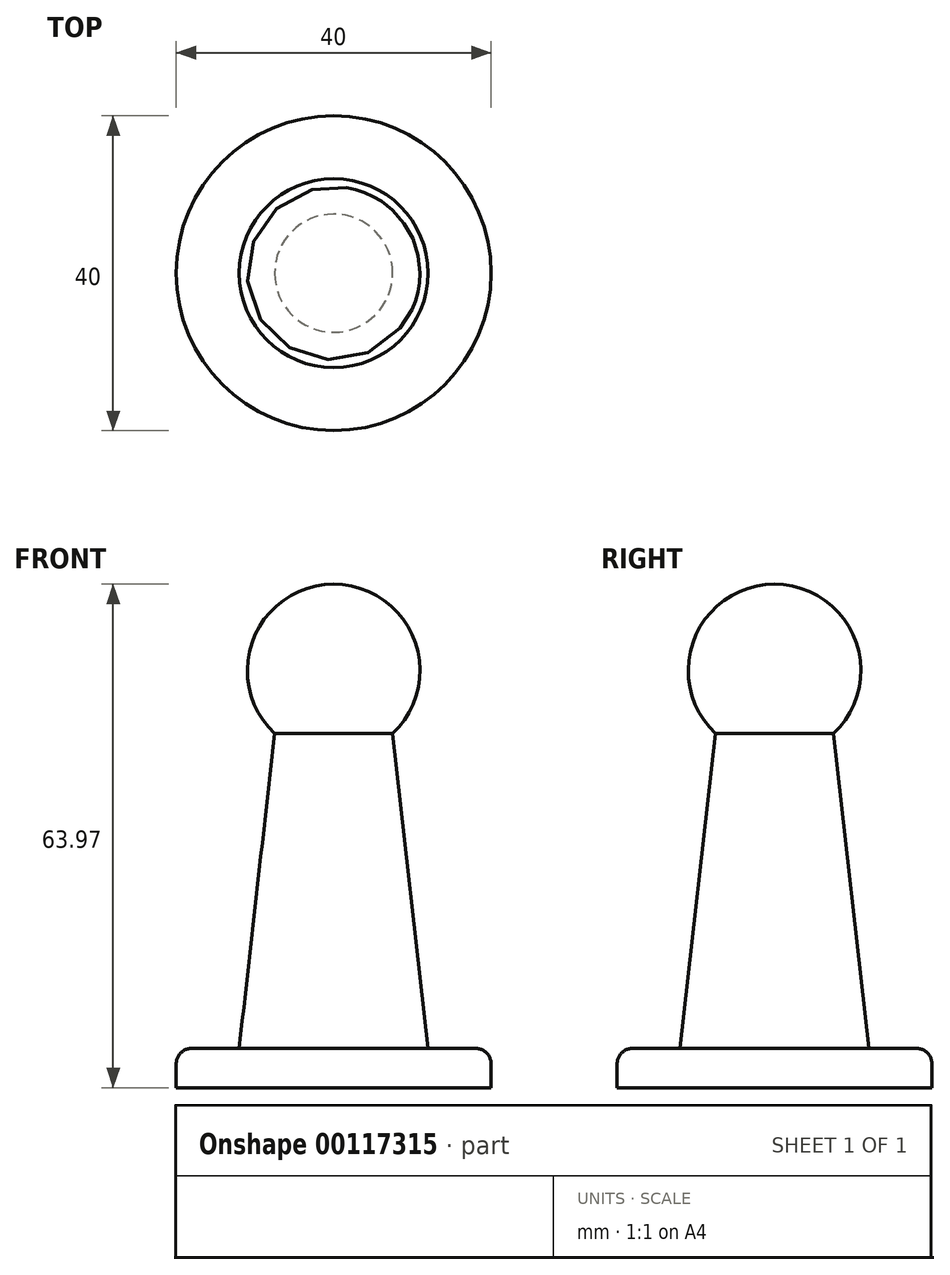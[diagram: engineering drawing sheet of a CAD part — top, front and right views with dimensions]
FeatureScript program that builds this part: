
annotation { "Feature Type Name" : "Feature", "Feature Type Description" : "" }
export const myFeature = defineFeature(function(context is Context, id is Id, definition is map)
    precondition{}
    {
        {
            var Q0;
            Q0=qCreatedBy(makeId("Front.planeOp"),FACE);
            var sketch = newSketch(context, id + "F0", { "sketchPlane" : qUnion([Q0])});
            skLineSegment(sketch, "E0.bottom", {"start": v(20, -2.5) * mm, "end": v(-20, -2.5) * mm, "construction": true});
            skLineSegment(sketch, "E0.top", {"start": v(20, 2.5) * mm, "end": v(-20, 2.5) * mm, "construction": true});
            skLineSegment(sketch, "E0.left", {"start": v(20, -2.5) * mm, "end": v(20, 2.5) * mm, "construction": true});
            skLineSegment(sketch, "E0.right", {"start": v(-20, -2.5) * mm, "end": v(-20, 2.5) * mm});
            skPoint(sketch, "E0.middle", {"position": v(0, 0) * mm});
            skLineSegment(sketch, "E1", {"start": v(-20, 2.5) * mm, "end": v(-12, 2.5) * mm});
            skLineSegment(sketch, "E2", {"start": v(20, 2.5) * mm, "end": v(12, 2.5) * mm, "construction": true});
            skLineSegment(sketch, "E3", {"start": v(0, 2.5) * mm, "end": v(0, 42.5) * mm, "construction": true});
            skLineSegment(sketch, "E4", {"start": v(0, 42.5) * mm, "end": v(7.5, 42.5) * mm, "construction": true});
            skLineSegment(sketch, "E5", {"start": v(0, 42.5) * mm, "end": v(-7.5, 42.5) * mm, "construction": true});
            skArc(sketch, "E6", {"start": v(7.5, 42.5) * mm, "mid": v(0, 61.47) * mm, "end": v(-7.5, 42.5) * mm, "construction": true});
            skLineSegment(sketch, "E7", {"start": v(-7.5, 42.5) * mm, "end": v(-12, 2.5) * mm});
            skLineSegment(sketch, "E8", {"start": v(7.5, 42.5) * mm, "end": v(12, 2.5) * mm, "construction": true});
            skLineSegment(sketch, "E9", {"start": v(0, -2.5) * mm, "end": v(0, 61.47) * mm});
            skArc(sketch, "E10", {"start": v(0, 61.47) * mm, "mid": v(-10.2, 54.53) * mm, "end": v(-7.5, 42.5) * mm});
            skLineSegment(sketch, "E11", {"start": v(-20, -2.5) * mm, "end": v(0, -2.5) * mm});
            skSolve(sketch);
        }
        {
            var Q0;
            Q0=qSketchRegion(id+"F0",true);
            var Q1;
            Q1=sQuery(id+"F0.wireOp",EDGE,"E3");
            revolve(context, id + "F1", {"entities" : qUnion([Q0]), "axis" : qUnion([Q1]), "revolveType" : RevolveType.FULL});
        }
        {
            var Q0;
            Q0=makeQuery(id+"F1.opRevolve","SWEPT_EDGE",EDGE,{"disambiguationData":[OSD([sQuery(id+"F0.wireOp",EDGE,"E0.right"),sQuery(id+"F0.wireOp",EDGE,"E1")])]});
            fillet(context, id + "F2", {"entities" : qUnion([Q0]), "radius" : 2 * mm, "tangentPropagation" : true, "allowEdgeOverflow" : false});
        }
    });
